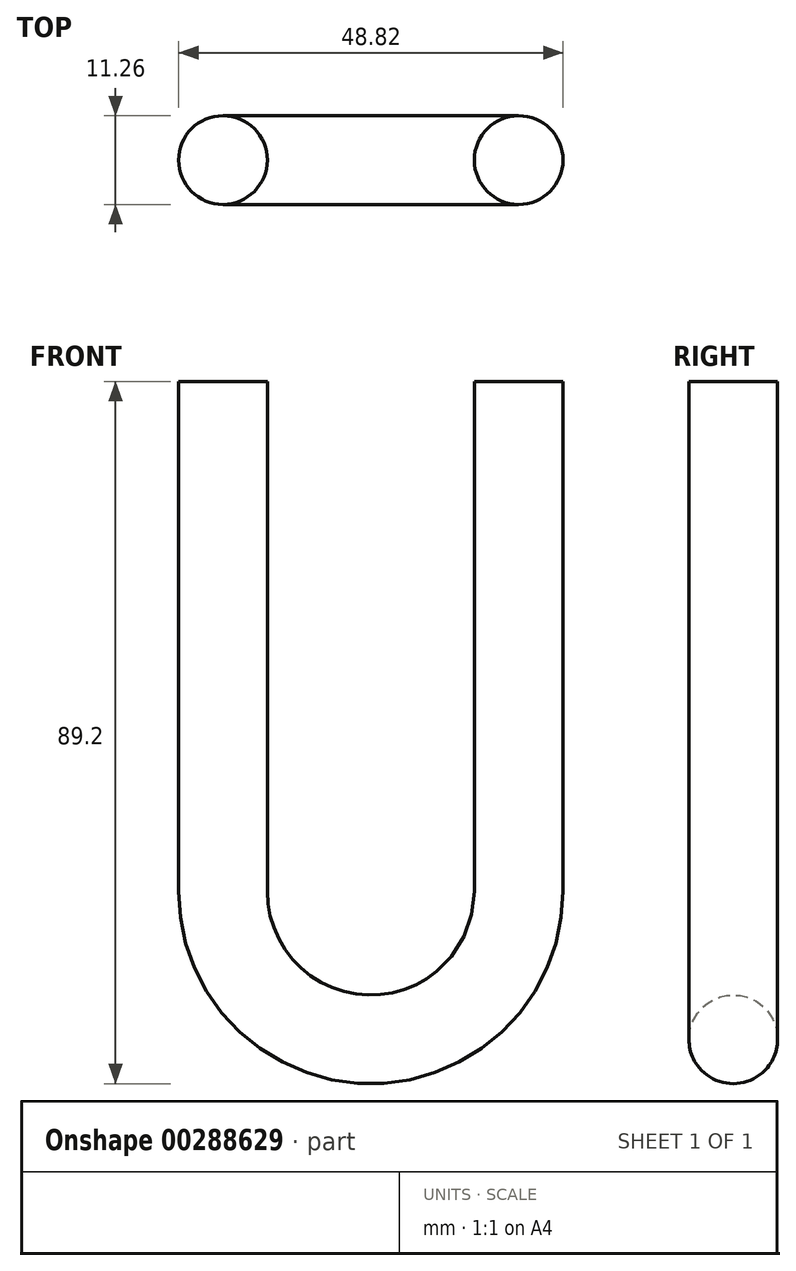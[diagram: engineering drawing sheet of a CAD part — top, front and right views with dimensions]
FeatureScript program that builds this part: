
annotation { "Feature Type Name" : "Feature", "Feature Type Description" : "" }
export const myFeature = defineFeature(function(context is Context, id is Id, definition is map)
    precondition{}
    {
        {
            var Q0;
            Q0=qCreatedBy(makeId("Front.planeOp"),FACE);
            var sketch = newSketch(context, id + "F0", { "sketchPlane" : qUnion([Q0])});
            skLineSegment(sketch, "E0", {"start": v(0, 0) * mm, "end": v(0, -64.79) * mm});
            skArc(sketch, "E1", {"start": v(0, -64.79) * mm, "mid": v(-18.78, -83.56) * mm, "end": v(-37.56, -64.79) * mm});
            skLineSegment(sketch, "E2", {"start": v(-37.56, -64.79) * mm, "end": v(-37.56, 0) * mm});
            skSolve(sketch);
        }
        {
            var Q0;
            Q0=qCreatedBy(makeId("Top.planeOp"),FACE);
            var sketch = newSketch(context, id + "F1", { "sketchPlane" : qUnion([Q0])});
            skCircle(sketch, "E3", {"center": v(0, 0) * mm, "radius": 5.63 * mm});
            skSolve(sketch);
        }
        {
            var Q0;
            Q0 = qSketchRegion(id + "F1", true);
            var Q1;
            Q1 = qConstructionFilter(qBodyType(qCreatedBy(id + "F0" ,EDGE), BodyType.WIRE), ConstructionObject.NO);
            sweep(context, id + "F2", {"profiles" : qUnion([Q0]), "path" : qUnion([Q1])});
        }
    });
